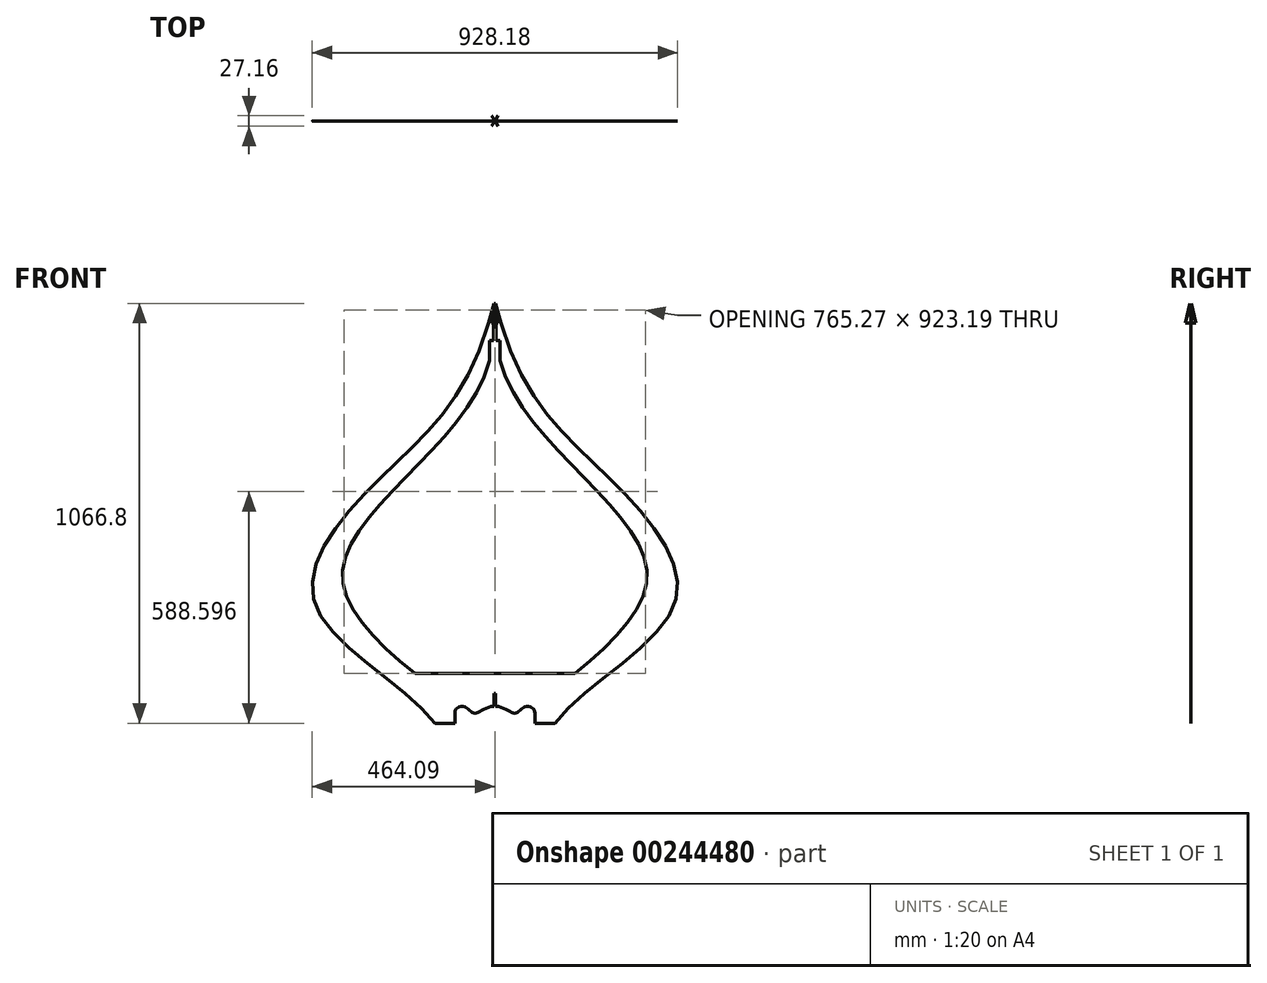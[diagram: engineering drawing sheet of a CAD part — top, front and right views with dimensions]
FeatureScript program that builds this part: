
annotation { "Feature Type Name" : "Feature", "Feature Type Description" : "" }
export const myFeature = defineFeature(function(context is Context, id is Id, definition is map)
    precondition{}
    {
        {
            assignVariable(context, id + "F0", {"name" : "thk", "anyValue" : .109});
        }
        {
            var Q0;
            Q0=qCreatedBy(makeId("Top.planeOp"),FACE);
            var sketch = newSketch(context, id + "F1", { "sketchPlane" : qUnion([Q0])});
            skCircle(sketch, "E0.cCircle", {"center": v(0, 0) * mm, "radius": 1.38 * mm, "construction": true});
            skLineSegment(sketch, "E0.0", {"start": v(1.38, 0) * mm, "end": v(0.7, -1.2) * mm});
            skLineSegment(sketch, "E0.1", {"start": v(0.7, -1.2) * mm, "end": v(-0.7, -1.2) * mm});
            skLineSegment(sketch, "E0.2", {"start": v(-0.7, -1.2) * mm, "end": v(-1.38, 0) * mm});
            skLineSegment(sketch, "E0.3", {"start": v(-1.38, 0) * mm, "end": v(-0.7, 1.2) * mm});
            skLineSegment(sketch, "E0.4", {"start": v(-0.7, 1.2) * mm, "end": v(0.7, 1.2) * mm});
            skLineSegment(sketch, "E0.5", {"start": v(0.7, 1.2) * mm, "end": v(1.38, 0) * mm});
            skSolve(sketch);
        }
        {
            var Q0;
            Q0=qCreatedBy(makeId("Front.planeOp"),FACE);
            var sketch = newSketch(context, id + "F2", { "sketchPlane" : qUnion([Q0])});
            skLineSegment(sketch, "E1", {"start": v(0, 0) * mm, "end": v(2.3, -8.55) * mm, "construction": true});
            skLineSegment(sketch, "E2.left", {"start": v(2.3, -25.16) * mm, "end": v(2.3, -58.38) * mm});
            skLineSegment(sketch, "E3", {"start": v(2.3, -58.38) * mm, "end": v(15.64, -58.38) * mm});
            skLineSegment(sketch, "E4", {"start": v(15.64, -58.38) * mm, "end": v(7.45, -27.79) * mm});
            skLineSegment(sketch, "E5", {"start": v(2.3, -25.16) * mm, "end": v(0, -25.16) * mm});
            skLineSegment(sketch, "E6", {"start": v(0, 0) * mm, "end": v(0, 5) * mm, "construction": true});
            skLineSegment(sketch, "E7.0", {"start": v(-1.38, 0) * mm, "end": v(1.38, 0) * mm, "construction": true});
            skLineSegment(sketch, "E8", {"start": v(2.3, -25.16) * mm, "end": v(4.57, -25.37) * mm, "construction": true});
            skLineSegment(sketch, "E9", {"start": v(6.85, -25.58) * mm, "end": v(7.45, -27.79) * mm});
            skLineSegment(sketch, "E10.MirrorCS", {"start": v(0, 0) * mm, "end": v(-2.3, -8.55) * mm, "construction": true});
            skLineSegment(sketch, "E11.MirrorCS", {"start": v(-6.85, -25.58) * mm, "end": v(-7.45, -27.79) * mm});
            skLineSegment(sketch, "E12.MirrorCS", {"start": v(-15.64, -58.38) * mm, "end": v(-7.45, -27.79) * mm});
            skLineSegment(sketch, "E13.MirrorCS", {"start": v(-2.3, -58.38) * mm, "end": v(-15.64, -58.38) * mm});
            skLineSegment(sketch, "E14.MirrorCS", {"start": v(-2.3, -25.16) * mm, "end": v(-2.3, -58.38) * mm});
            skLineSegment(sketch, "E15.MirrorCS", {"start": v(-2.3, -25.16) * mm, "end": v(0, -25.16) * mm});
            skCircle(sketch, "E16", {"center": v(2.3, -25.16) * mm, "radius": 2.3 * mm, "construction": true});
            skCircle(sketch, "E17", {"center": v(6.85, -25.58) * mm, "radius": 2.3 * mm, "construction": true});
            skLineSegment(sketch, "E18", {"start": v(-2.3, -8.55) * mm, "end": v(2.3, -8.55) * mm});
            skLineSegment(sketch, "E19", {"start": v(-2.3, -8.55) * mm, "end": v(-6.85, -25.58) * mm});
            skLineSegment(sketch, "E20", {"start": v(2.3, -8.55) * mm, "end": v(6.85, -25.58) * mm});
            skSolve(sketch);
        }
        {
            var Q0;
            Q0=qCreatedBy(makeId("Top.planeOp"),FACE);
            var Q1;
            Q1=sQuery(id+"F2.wireOp",VERTEX,"E1.end");
            cPlane(context, id + "F3", {"entities" : qUnion([Q0, Q1]), "cplaneType" : CPlaneType.PLANE_POINT, "offset" : 25.4 * mm, "width" : 152.4 * mm, "height" : 152.4 * mm});
        }
        {
            var Q0;
            Q0=qCreatedBy(makeId("Top.planeOp"),FACE);
            var Q1;
            Q1=sQuery(id+"F2.wireOp",VERTEX,"E4.end");
            cPlane(context, id + "F4", {"entities" : qUnion([Q0, Q1]), "cplaneType" : CPlaneType.PLANE_POINT, "offset" : 25.4 * mm, "width" : 152.4 * mm, "height" : 152.4 * mm});
        }
        {
            var Q0;
            Q0=qCreatedBy(id+"F4.planeOp",FACE);
            var sketch = newSketch(context, id + "F5", { "sketchPlane" : qUnion([Q0])});
            skCircle(sketch, "E21.cCircle", {"center": v(0, 0) * mm, "radius": 7.45 * mm, "construction": true});
            skLineSegment(sketch, "E21.0", {"start": v(7.45, 0) * mm, "end": v(3.72, -6.45) * mm});
            skLineSegment(sketch, "E21.1", {"start": v(3.72, -6.45) * mm, "end": v(-3.72, -6.45) * mm});
            skLineSegment(sketch, "E21.2", {"start": v(-3.72, -6.45) * mm, "end": v(-7.45, 0) * mm});
            skLineSegment(sketch, "E21.3", {"start": v(-7.45, 0) * mm, "end": v(-3.72, 6.45) * mm});
            skLineSegment(sketch, "E21.4", {"start": v(-3.72, 6.45) * mm, "end": v(3.72, 6.45) * mm});
            skLineSegment(sketch, "E21.5", {"start": v(3.72, 6.45) * mm, "end": v(7.45, 0) * mm});
            skSolve(sketch);
        }
        {
            var Q0;
            Q0=qCreatedBy(makeId("Top.planeOp"),FACE);
            var Q1;
            Q1=sQuery(id+"F2.wireOp",VERTEX,"E13.MirrorCS.start");
            cPlane(context, id + "F6", {"entities" : qUnion([Q0, Q1]), "cplaneType" : CPlaneType.PLANE_POINT, "offset" : 25.4 * mm, "width" : 152.4 * mm, "height" : 152.4 * mm});
        }
        {
            var Q0;
            Q0=qCreatedBy(id+"F6.planeOp",FACE);
            var sketch = newSketch(context, id + "F7", { "sketchPlane" : qUnion([Q0])});
            skCircle(sketch, "E22.cCircle", {"center": v(0, 0) * mm, "radius": 15.64 * mm, "construction": true});
            skLineSegment(sketch, "E22.0", {"start": v(-15.64, 0) * mm, "end": v(-7.82, 13.55) * mm});
            skLineSegment(sketch, "E22.1", {"start": v(-7.82, 13.55) * mm, "end": v(7.82, 13.55) * mm});
            skLineSegment(sketch, "E22.2", {"start": v(7.82, 13.55) * mm, "end": v(15.64, 0) * mm});
            skLineSegment(sketch, "E22.3", {"start": v(15.64, 0) * mm, "end": v(7.82, -13.55) * mm});
            skLineSegment(sketch, "E22.4", {"start": v(7.82, -13.55) * mm, "end": v(-7.82, -13.55) * mm});
            skLineSegment(sketch, "E22.5", {"start": v(-7.82, -13.55) * mm, "end": v(-15.64, 0) * mm});
            skSolve(sketch);
        }
        {
            var Q0;
            Q0=sQuery(id+"F2.wireOp",EDGE,"E6");
            var Q1;
            Q1=sQuery(id+"F1.wireOp",VERTEX,"E0.5.start");
            cPlane(context, id + "F8", {"entities" : qUnion([Q0, Q1]), "cplaneType" : CPlaneType.LINE_ANGLE, "offset" : 25.4 * mm, "angle" : 0 * degree, "width" : 152.4 * mm, "height" : 152.4 * mm});
        }
        {
            var Q0;
            Q0=qCreatedBy(id+"F8.planeOp",FACE);
            var sketch = newSketch(context, id + "F9", { "sketchPlane" : qUnion([Q0])});
            skLineSegment(sketch, "E23.1", {"start": v(2.3, -8.55) * mm, "end": v(7.45, -27.79) * mm});
            skLineSegment(sketch, "E23.2", {"start": v(15.64, -58.38) * mm, "end": v(7.45, -27.79) * mm});
            skLineSegment(sketch, "E24.0", {"start": v(0, 0) * mm, "end": v(0, 5) * mm, "construction": true});
            skLineSegment(sketch, "E25", {"start": v(2.3, -8.55) * mm, "end": v(2.3, -25.16) * mm});
            skLineSegment(sketch, "E26", {"start": v(2.3, -25.16) * mm, "end": v(0, -25.16) * mm});
            skLineSegment(sketch, "E27", {"start": v(0, -41.77) * mm, "end": v(2.3, -41.77) * mm});
            skLineSegment(sketch, "E28", {"start": v(2.3, -41.77) * mm, "end": v(2.3, -58.38) * mm});
            skLineSegment(sketch, "E29.0", {"start": v(2.3, -58.38) * mm, "end": v(15.64, -58.38) * mm});
            skLineSegment(sketch, "E30.MirrorCS", {"start": v(0, -41.77) * mm, "end": v(-2.3, -41.77) * mm});
            skLineSegment(sketch, "E31.MirrorCS", {"start": v(-2.3, -41.77) * mm, "end": v(-2.3, -58.38) * mm});
            skLineSegment(sketch, "E32.MirrorCS", {"start": v(-2.3, -58.38) * mm, "end": v(-15.64, -58.38) * mm});
            skLineSegment(sketch, "E33.MirrorCS", {"start": v(-15.64, -58.38) * mm, "end": v(-7.45, -27.79) * mm});
            skLineSegment(sketch, "E34.MirrorCS", {"start": v(-2.3, -8.55) * mm, "end": v(-7.45, -27.79) * mm});
            skLineSegment(sketch, "E35.MirrorCS", {"start": v(-2.3, -8.55) * mm, "end": v(-2.3, -25.16) * mm});
            skLineSegment(sketch, "E36.MirrorCS", {"start": v(-2.3, -25.16) * mm, "end": v(0, -25.16) * mm});
            skSolve(sketch);
        }
        {
            var Q0;
            Q0=sQuery(id+"F2.wireOp",EDGE,"E6");
            var Q1;
            Q1=sQuery(id+"F1.wireOp",VERTEX,"E0.1.start");
            cPlane(context, id + "F10", {"entities" : qUnion([Q0, Q1]), "cplaneType" : CPlaneType.LINE_ANGLE, "offset" : 25.4 * mm, "angle" : 0 * degree, "width" : 152.4 * mm, "height" : 152.4 * mm});
        }
        {
            var Q0;
            Q0=qCreatedBy(id+"F10.planeOp",FACE);
            var sketch = newSketch(context, id + "F11", { "sketchPlane" : qUnion([Q0])});
            skLineSegment(sketch, "E37.0", {"start": v(15.64, -58.38) * mm, "end": v(7.45, -27.79) * mm});
            skLineSegment(sketch, "E37.1", {"start": v(1.15, -58.38) * mm, "end": v(15.64, -58.38) * mm});
            skLineSegment(sketch, "E37.2", {"start": v(2.3, -8.55) * mm, "end": v(7.45, -27.79) * mm});
            skLineSegment(sketch, "E37.3", {"start": v(0, 0) * mm, "end": v(0, 5) * mm, "construction": true});
            skLineSegment(sketch, "E38", {"start": v(2.3, -41.77) * mm, "end": v(0, -41.77) * mm});
            skLineSegment(sketch, "E39", {"start": v(1.15, -58.38) * mm, "end": v(0, -58.38) * mm});
            skLineSegment(sketch, "E40", {"start": v(2.3, -41.77) * mm, "end": v(2.3, -8.55) * mm});
            skLineSegment(sketch, "E41.MirrorCS", {"start": v(-2.3, -41.77) * mm, "end": v(0, -41.77) * mm});
            skLineSegment(sketch, "E42.MirrorCS", {"start": v(-2.3, -41.77) * mm, "end": v(-2.3, -8.55) * mm});
            skLineSegment(sketch, "E43.MirrorCS", {"start": v(-2.3, -8.55) * mm, "end": v(-7.45, -27.79) * mm});
            skLineSegment(sketch, "E44.MirrorCS", {"start": v(-15.64, -58.38) * mm, "end": v(-7.45, -27.79) * mm});
            skLineSegment(sketch, "E45.MirrorCS", {"start": v(-1.15, -58.38) * mm, "end": v(-15.64, -58.38) * mm});
            skLineSegment(sketch, "E46.MirrorCS", {"start": v(-1.15, -58.38) * mm, "end": v(0, -58.38) * mm});
            skSolve(sketch);
        }
        {
            var Q0;
            Q0 = qSketchRegion(id + "F2", true);
            extrude(context, id + "F12", {"entities" : qUnion([Q0]), "depth" : (getVariable(context, 'thk')) * mm, "symmetric" : true});
        }
        {
            var Q0;
            Q0 = qSketchRegion(id + "F9", true);
            extrude(context, id + "F13", {"entities" : qUnion([Q0]), "depth" : (getVariable(context, 'thk')) * mm, "symmetric" : true});
        }
        {
            var Q0;
            Q0 = qSketchRegion(id + "F11", true);
            extrude(context, id + "F14", {"entities" : qUnion([Q0]), "depth" : (getVariable(context, 'thk')) * mm, "symmetric" : true});
        }
        {
            var Q0;
            Q0=qCreatedBy(makeId("Front.planeOp"),FACE);
            var sketch = newSketch(context, id + "F15", { "sketchPlane" : qUnion([Q0])});
            skLineSegment(sketch, "E47", {"start": v(0, -8.55) * mm, "end": v(0, -1075.35) * mm, "construction": true});
            skLineSegment(sketch, "E48", {"start": v(-457.2, -770.55) * mm, "end": v(457.2, -770.55) * mm, "construction": true});
            skPoint(sketch, "E49", {"position": v(0, -770.55) * mm});
            skFitSpline(sketch, "E50", {"points": [v(152.4, -1075.35) * mm, v(457.2, -770.55) * mm, v(304.8, -465.75) * mm, v(15.64, -58.38) * mm], "startDerivative": vector(643.21, 886.76) * mm, "endDerivative": vector(-495.74, 1751.28) * mm});
            skLineSegment(sketch, "E51", {"start": v(0, -948.35) * mm, "end": v(203.2, -948.35) * mm});
            skFitSpline(sketch, "E52", {"points": [v(203.2, -948.35) * mm, v(386.92, -704.57) * mm, v(238.34, -462.8) * mm, v(13.34, -153.63) * mm], "startDerivative": vector(901.41, 718.64) * mm, "endDerivative": vector(-263.23, 977.08) * mm});
            skLineSegment(sketch, "E53", {"start": v(152.4, -1075.35) * mm, "end": v(101.6, -1075.35) * mm});
            skLineSegment(sketch, "E54", {"start": v(101.6, -1075.35) * mm, "end": v(101.6, -1049.95) * mm});
            skFitSpline(sketch, "E55", {"points": [v(101.6, -1049.95) * mm, v(76.2, -1034.07) * mm, v(50.8, -1049.95) * mm, v(2.3, -1032.37) * mm], "startDerivative": vector(0, 157.76) * mm, "endDerivative": vector(-174.97, 0) * mm});
            skLineSegment(sketch, "E56", {"start": v(3.17, -102.83) * mm, "end": v(3.17, -58.38) * mm});
            skLineSegment(sketch, "E57", {"start": v(15.64, -58.38) * mm, "end": v(3.17, -58.38) * mm});
            skLineSegment(sketch, "E58", {"start": v(13.34, -153.63) * mm, "end": v(13.34, -102.83) * mm});
            skLineSegment(sketch, "E59", {"start": v(13.34, -102.83) * mm, "end": v(3.17, -102.83) * mm});
            skLineSegment(sketch, "E60", {"start": v(0, -999.15) * mm, "end": v(2.3, -999.15) * mm});
            skLineSegment(sketch, "E61", {"start": v(2.3, -999.15) * mm, "end": v(2.3, -1032.37) * mm});
            skLineSegment(sketch, "E62.MirrorCS", {"start": v(-3.17, -102.83) * mm, "end": v(-3.17, -58.38) * mm});
            skLineSegment(sketch, "E63.MirrorCS", {"start": v(-15.64, -58.38) * mm, "end": v(-3.17, -58.38) * mm});
            skFitSpline(sketch, "E64.MirrorCS", {"points": [v(-152.4, -1075.35) * mm, v(-457.2, -770.55) * mm, v(-304.8, -465.75) * mm, v(-15.64, -58.38) * mm], "startDerivative": vector(-643.21, 886.76) * mm, "endDerivative": vector(495.74, 1751.28) * mm});
            skLineSegment(sketch, "E65.MirrorCS", {"start": v(-13.34, -102.83) * mm, "end": v(-3.17, -102.83) * mm});
            skLineSegment(sketch, "E66.MirrorCS", {"start": v(-13.34, -153.63) * mm, "end": v(-13.34, -102.83) * mm});
            skFitSpline(sketch, "E67.MirrorCS", {"points": [v(-203.2, -948.35) * mm, v(-386.92, -704.57) * mm, v(-238.34, -462.8) * mm, v(-13.34, -153.63) * mm], "startDerivative": vector(-901.41, 718.64) * mm, "endDerivative": vector(263.23, 977.08) * mm});
            skLineSegment(sketch, "E68.MirrorCS", {"start": v(0, -948.35) * mm, "end": v(-203.2, -948.35) * mm});
            skLineSegment(sketch, "E69.MirrorCS", {"start": v(0, -999.15) * mm, "end": v(-2.3, -999.15) * mm});
            skLineSegment(sketch, "E70.MirrorCS", {"start": v(-2.3, -999.15) * mm, "end": v(-2.3, -1032.37) * mm});
            skFitSpline(sketch, "E71.MirrorCS", {"points": [v(-101.6, -1049.95) * mm, v(-76.2, -1034.07) * mm, v(-50.8, -1049.95) * mm, v(-2.3, -1032.37) * mm], "startDerivative": vector(0, 157.76) * mm, "endDerivative": vector(174.97, 0) * mm});
            skLineSegment(sketch, "E72.MirrorCS", {"start": v(-101.6, -1075.35) * mm, "end": v(-101.6, -1049.95) * mm});
            skLineSegment(sketch, "E73.MirrorCS", {"start": v(-152.4, -1075.35) * mm, "end": v(-101.6, -1075.35) * mm});
            skSolve(sketch);
        }
        {
            var Q0;
            Q0=makeQuery(id+"F15.imprint","IMPRINT",FACE,{"disambiguationData":[TD([[makeQuery(id+"F15.imprint","IMPRINT",EDGE,{"derivedFrom":sQuery(id+"F15.wireOp",EDGE,"E50")}),1.0]])]});
            extrude(context, id + "F16", {"entities" : qUnion([Q0]), "operationType" : NewBodyOperationType.ADD, "depth" : (getVariable(context, 'thk')) * mm, "symmetric" : true});
        }
    });
